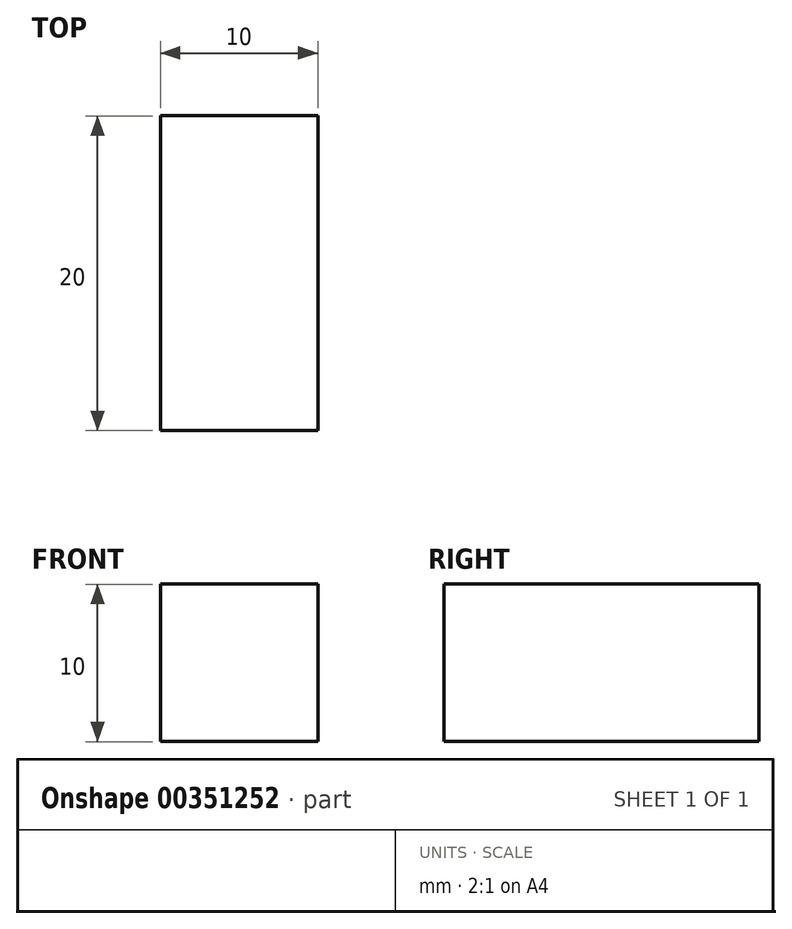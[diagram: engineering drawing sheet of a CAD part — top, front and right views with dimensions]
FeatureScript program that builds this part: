
annotation { "Feature Type Name" : "Feature", "Feature Type Description" : "" }
export const myFeature = defineFeature(function(context is Context, id is Id, definition is map)
    precondition{}
    {
        {
            var Q0;
            Q0=qCreatedBy(makeId("Right.planeOp"),FACE);
            var sketch = newSketch(context, id + "F0", { "sketchPlane" : qUnion([Q0])});
            skLineSegment(sketch, "E0.bottom", {"start": v(-79.33, -41.7) * mm, "end": v(-99.33, -41.7) * mm});
            skLineSegment(sketch, "E0.top", {"start": v(-79.33, -51.7) * mm, "end": v(-99.33, -51.7) * mm});
            skLineSegment(sketch, "E0.left", {"start": v(-79.33, -41.7) * mm, "end": v(-79.33, -51.7) * mm});
            skLineSegment(sketch, "E0.right", {"start": v(-99.33, -41.7) * mm, "end": v(-99.33, -51.7) * mm});
            skSolve(sketch);
        }
        {
            var Q0;
            Q0=makeQuery(id+"F0.imprint","IMPRINT",FACE,{"disambiguationData":[TD([[makeQuery(id+"F0.imprint","IMPRINT",EDGE,{"derivedFrom":sQuery(id+"F0.wireOp",EDGE,"E0.bottom")}),1.0]])]});
            extrude(context, id + "F1", {"entities" : qUnion([Q0]), "depth" : 10 * mm});
        }
    });
